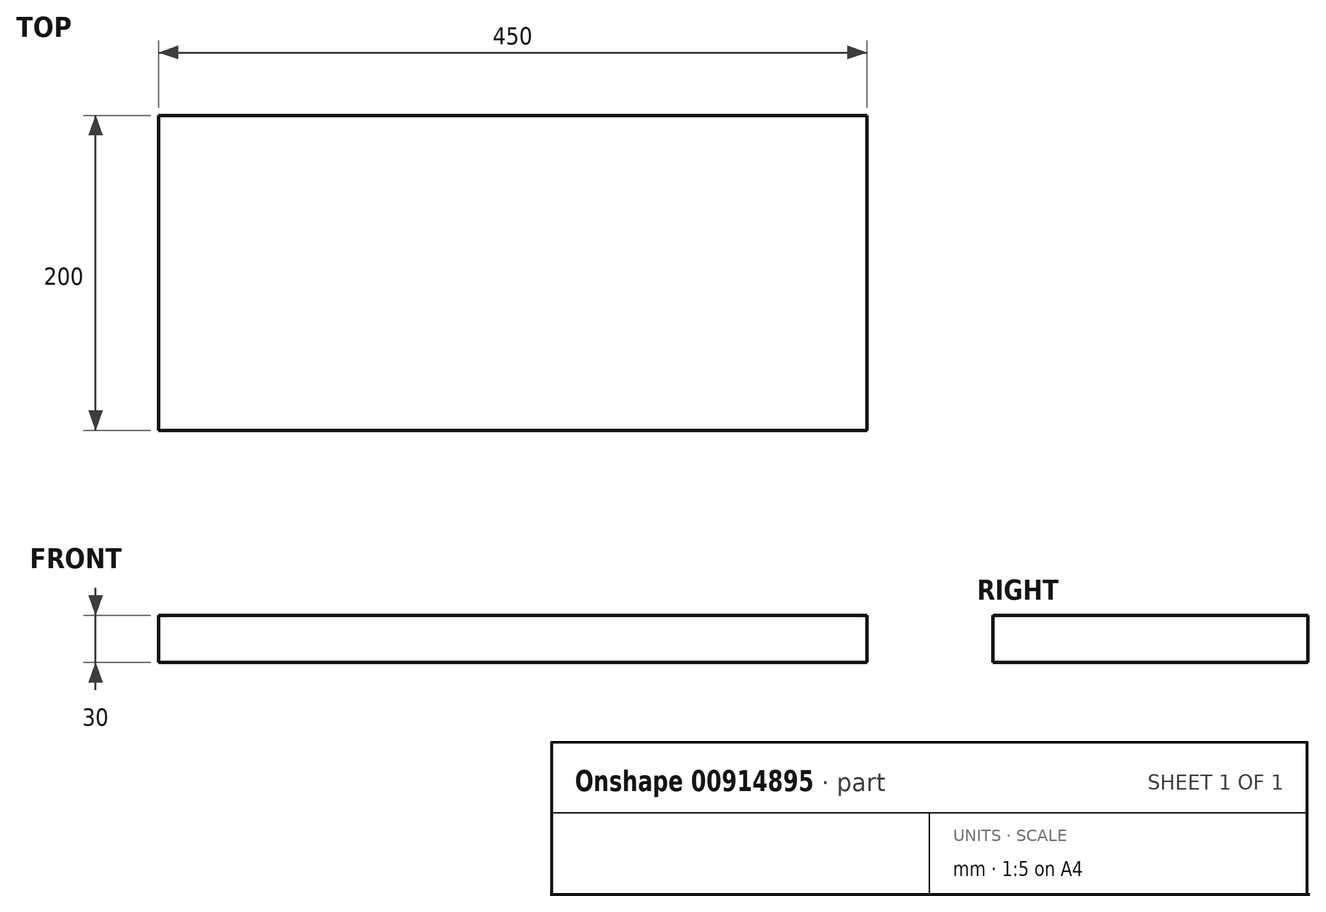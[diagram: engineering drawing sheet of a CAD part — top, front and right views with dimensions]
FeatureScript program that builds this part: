
annotation { "Feature Type Name" : "Feature", "Feature Type Description" : "" }
export const myFeature = defineFeature(function(context is Context, id is Id, definition is map)
    precondition{}
    {
        {
            var Q0;
            Q0=qCreatedBy(makeId("Top.planeOp"),FACE);
            var sketch = newSketch(context, id + "F0", { "sketchPlane" : qUnion([Q0])});
            skLineSegment(sketch, "E0.bottom", {"start": v(225, -100) * mm, "end": v(-225, -100) * mm});
            skLineSegment(sketch, "E0.top", {"start": v(225, 100) * mm, "end": v(-225, 100) * mm});
            skLineSegment(sketch, "E0.left", {"start": v(225, -100) * mm, "end": v(225, 100) * mm});
            skLineSegment(sketch, "E0.right", {"start": v(-225, -100) * mm, "end": v(-225, 100) * mm});
            skPoint(sketch, "E0.middle", {"position": v(0, 0) * mm});
            skSolve(sketch);
        }
        {
            var Q0;
            Q0 = qSketchRegion(id + "F0", true);
            extrude(context, id + "F1", {"entities" : qUnion([Q0]), "depth" : 30 * mm, "offsetDistance" : 25 * mm});
        }
    });
